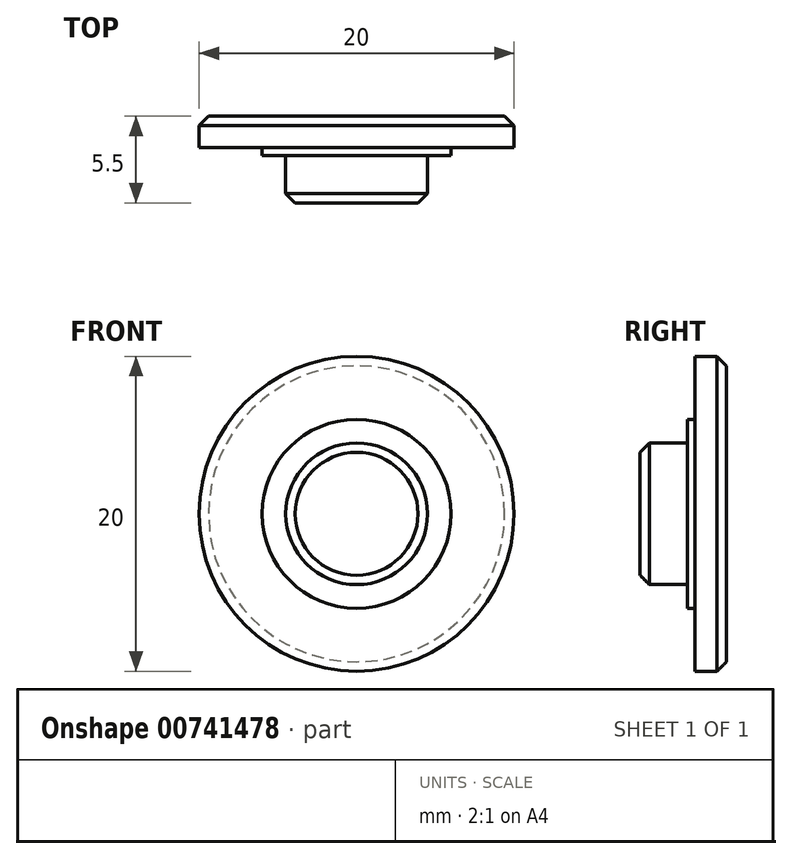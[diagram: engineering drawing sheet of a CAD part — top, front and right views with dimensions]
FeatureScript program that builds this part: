
annotation { "Feature Type Name" : "Feature", "Feature Type Description" : "" }
export const myFeature = defineFeature(function(context is Context, id is Id, definition is map)
    precondition{}
    {
        {
            var Q0;
            Q0=qCreatedBy(makeId("Front.planeOp"),FACE);
            var sketch = newSketch(context, id + "F0", { "sketchPlane" : qUnion([Q0])});
            skCircle(sketch, "E0", {"center": v(0, 0) * mm, "radius": 10 * mm});
            skSolve(sketch);
        }
        {
            var Q0;
            Q0 = qSketchRegion(id + "F0", true);
            extrude(context, id + "F1", {"entities" : qUnion([Q0]), "depth" : 2 * mm, "offsetDistance" : 25 * mm});
        }
        {
            var Q0;
            Q0=makeQuery(id+"F1.opExtrude","CAP_FACE",FACE,{"disambiguationData":[OSD([sQuery(id+"F0.wireOp",EDGE,"E0")])],"isStart":false});
            var sketch = newSketch(context, id + "F2", { "sketchPlane" : qUnion([Q0])});
            skCircle(sketch, "E1", {"center": v(0, 0) * mm, "radius": 4.5 * mm});
            skSolve(sketch);
        }
        {
            var Q0;
            Q0 = qSketchRegion(id + "F2", true);
            extrude(context, id + "F3", {"entities" : qUnion([Q0]), "operationType" : NewBodyOperationType.ADD, "depth" : 3.5 * mm, "offsetDistance" : 25 * mm});
        }
        {
            var Q0;
            Q0=makeQuery(id+"F1.opExtrude","CAP_FACE",FACE,{"disambiguationData":[OSD([sQuery(id+"F0.wireOp",EDGE,"E0")])],"isStart":false});
            var sketch = newSketch(context, id + "F4", { "sketchPlane" : qUnion([Q0])});
            skSolve(sketch);
        }
        {
            var Q0;
            Q0=makeQuery(id+"F4.imprint","IMPRINT",FACE,{"disambiguationData":[TD([[makeQuery(id+"F4.imprint","IMPRINT",EDGE,{"derivedFrom":makeQuery(id+"F1.opExtrude","CAP_EDGE",EDGE,{"disambiguationData":[OSD([sQuery(id+"F0.wireOp",EDGE,"E0")])],"isStart":false})}),1.0]])]});
            var sketch = newSketch(context, id + "F5", { "sketchPlane" : qUnion([Q0])});
            skCircle(sketch, "E2", {"center": v(0, 0) * mm, "radius": 6 * mm});
            skSolve(sketch);
        }
        {
            var Q0;
            Q0 = qSketchRegion(id + "F5", true);
            extrude(context, id + "F6", {"entities" : qUnion([Q0]), "operationType" : NewBodyOperationType.ADD, "depth" : 0.5 * mm, "offsetDistance" : 25 * mm});
        }
        {
            var Q0;
            Q0=makeQuery(id+"F1.opExtrude","CAP_EDGE",EDGE,{"disambiguationData":[OSD([sQuery(id+"F0.wireOp",EDGE,"E0")])],"isStart":true});
            var Q1;
            Q1=makeQuery(id+"F3.opExtrude","CAP_EDGE",EDGE,{"disambiguationData":[OSD([sQuery(id+"F2.wireOp",EDGE,"E1")])],"isStart":false});
            chamfer(context, id + "F7", {"entities" : qUnion([Q0, Q1]), "width" : 0.6 * mm, "tangentPropagation" : true});
        }
    });
